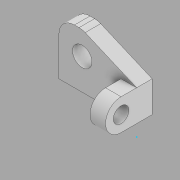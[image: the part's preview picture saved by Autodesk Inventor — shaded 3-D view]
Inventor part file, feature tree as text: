
AUTODESK INVENTOR PART (.ipt)
format: ipt  version: 2020 (Build 240168000, 168)  size: 122,880 bytes
history: native  units: mm
features: sketch x3, extrude x2, other x1
ambient origin geometry x8: Origin, YZ Plane, XZ Plane, XY Plane, X Axis, Y Axis, Z Axis, Center Point
bodies: Body1 (feature_tree)
feature tree (6):
  other  "Sólido1"
  extrude  "Extrusión1"  Depth=7.0mm
  extrude  "Extrusión2"  Depth=7.0mm
  sketch  "Boceto3"  dims[d4=3.0mm d5=2.5mm d6=3.0mm d7=4.0mm d8=2.0mm d9=0.0mm d10=2.0mm d11=6.0mm d12=4.0mm d13=2.0mm d14=2.0mm d15=2.0mm d16=2.0mm d17=2.0mm d18=0.0mm]
  sketch  "Boceto1"  dims[d0=10.0mm d1=7.0mm]
  sketch  "Boceto2"  dims[d2=2.0mm d3=7.0mm]
